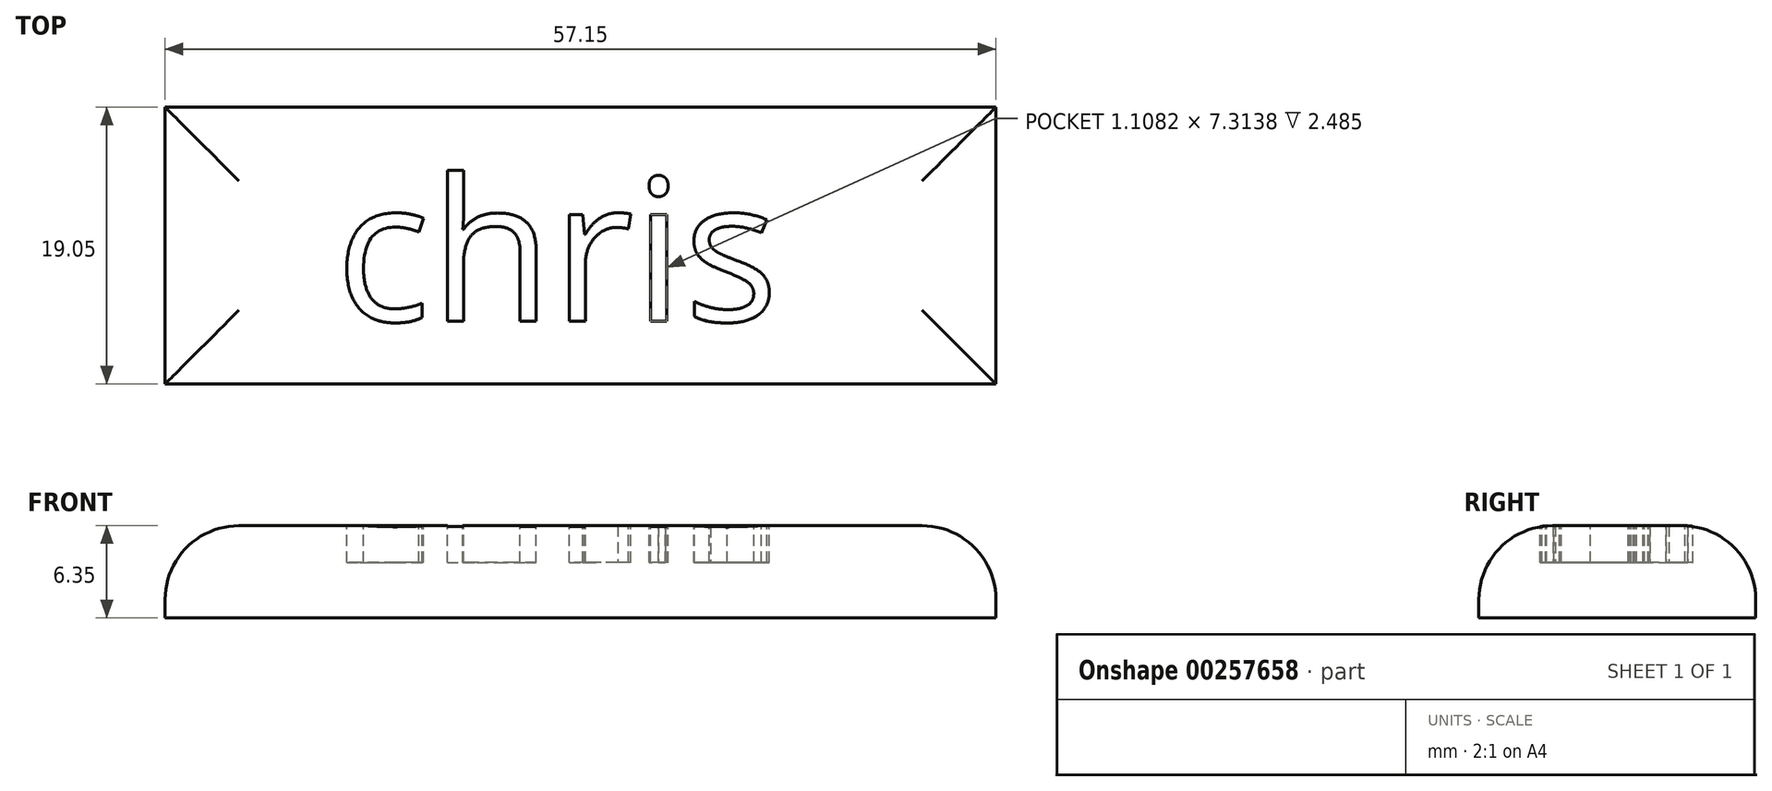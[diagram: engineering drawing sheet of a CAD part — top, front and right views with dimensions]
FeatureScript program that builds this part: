
annotation { "Feature Type Name" : "Feature", "Feature Type Description" : "" }
export const myFeature = defineFeature(function(context is Context, id is Id, definition is map)
    precondition{}
    {
        {
            var Q0;
            Q0=qCreatedBy(makeId("Top.planeOp"),FACE);
            var sketch = newSketch(context, id + "F0", { "sketchPlane" : qUnion([Q0])});
            skLineSegment(sketch, "E0.bottom", {"start": v(-26.13, 4.88) * mm, "end": v(31.02, 4.88) * mm});
            skLineSegment(sketch, "E0.top", {"start": v(-26.13, -14.17) * mm, "end": v(31.02, -14.17) * mm});
            skLineSegment(sketch, "E0.left", {"start": v(-26.13, 4.88) * mm, "end": v(-26.13, -14.17) * mm});
            skLineSegment(sketch, "E0.right", {"start": v(31.02, 4.88) * mm, "end": v(31.02, -14.17) * mm});
            skSolve(sketch);
        }
        {
            var Q0;
            Q0 = qSketchRegion(id + "F0", true);
            extrude(context, id + "F1", {"entities" : qUnion([Q0]), "depth" : 6.35 * mm});
        }
        {
            var Q0;
            Q0=makeQuery(id+"F1.opExtrude","CAP_FACE",FACE,{"disambiguationData":[OSD([sQuery(id+"F0.wireOp",EDGE,"E0.bottom"),sQuery(id+"F0.wireOp",EDGE,"E0.top"),sQuery(id+"F0.wireOp",EDGE,"E0.left"),sQuery(id+"F0.wireOp",EDGE,"E0.right")])],"isStart":false});
            var sketch = newSketch(context, id + "F2", { "sketchPlane" : qUnion([Q0])});
            skText(sketch, "E1", { "text": "chris", "fontName": "OpenSans-Regular.ttf"});
            const initialGuessF2  = {"E1": [-0.01439, -0.00984, 1, 0, 0.00984]};
            skSetInitialGuess(sketch, initialGuessF2);
            skSolve(sketch);
        }
        {
            var Q0;
            Q0 = qSketchRegion(id + "F2", true);
            extrude(context, id + "F3", {"entities" : qUnion([Q0]), "operationType" : NewBodyOperationType.REMOVE, "oppositeDirection" : true, "depth" : 2.54 * mm});
        }
        {
            var Q0;
            Q0=makeQuery(id+"F1.opExtrude","CAP_EDGE",EDGE,{"disambiguationData":[OSD([sQuery(id+"F0.wireOp",EDGE,"E0.bottom")])],"isStart":false});
            var Q1;
            Q1=makeQuery(id+"F1.opExtrude","CAP_EDGE",EDGE,{"disambiguationData":[OSD([sQuery(id+"F0.wireOp",EDGE,"E0.left")])],"isStart":false});
            var Q2;
            Q2=makeQuery(id+"F1.opExtrude","CAP_EDGE",EDGE,{"disambiguationData":[OSD([sQuery(id+"F0.wireOp",EDGE,"E0.top")])],"isStart":false});
            var Q3;
            Q3=makeQuery(id+"F1.opExtrude","CAP_EDGE",EDGE,{"disambiguationData":[OSD([sQuery(id+"F0.wireOp",EDGE,"E0.right")])],"isStart":false});
            fillet(context, id + "F4", {"entities" : qUnion([Q0, Q1, Q2, Q3]), "radius" : 5.08 * mm, "tangentPropagation" : true, "allowEdgeOverflow" : false});
        }
    });
